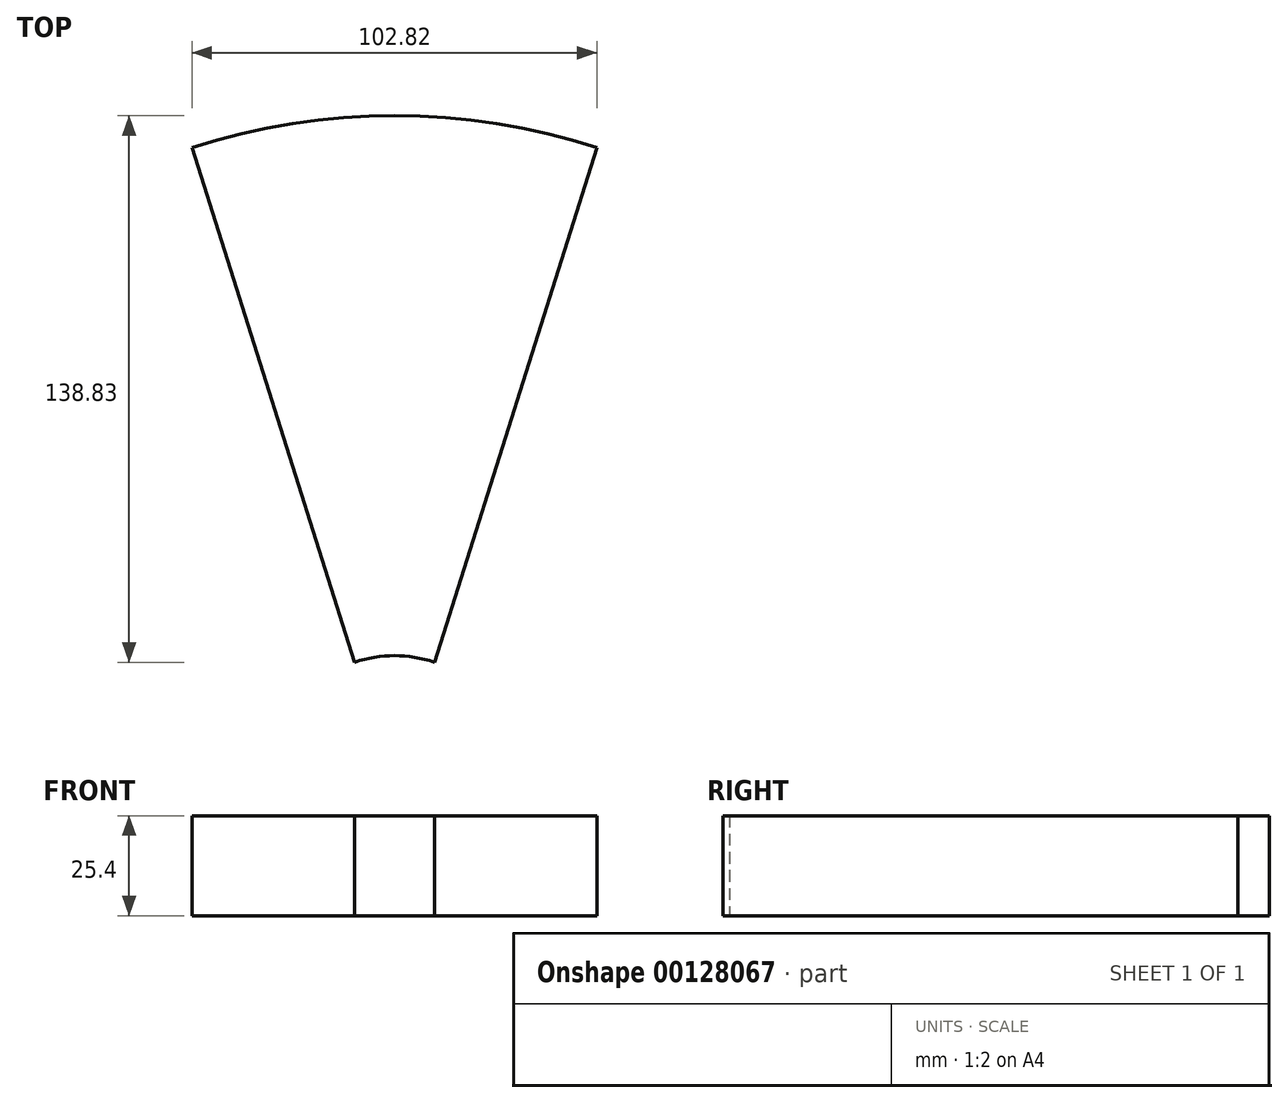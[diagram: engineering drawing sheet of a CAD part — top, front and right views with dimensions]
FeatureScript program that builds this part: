
annotation { "Feature Type Name" : "Feature", "Feature Type Description" : "" }
export const myFeature = defineFeature(function(context is Context, id is Id, definition is map)
    precondition{}
    {
        {
            var Q0;
            Q0=qCreatedBy(makeId("Top.planeOp"),FACE);
            var sketch = newSketch(context, id + "F0", { "sketchPlane" : qUnion([Q0])});
            skArc(sketch, "E0", {"start": v(10.16, 30.08) * mm, "mid": v(0, 31.75) * mm, "end": v(-10.16, 30.08) * mm});
            skArc(sketch, "E1", {"start": v(51.4, 160.9) * mm, "mid": v(0, 168.9) * mm, "end": v(-51.4, 160.9) * mm});
            skLineSegment(sketch, "E2", {"start": v(10.16, 30.08) * mm, "end": v(51.4, 160.9) * mm});
            skLineSegment(sketch, "E3", {"start": v(-51.4, 160.9) * mm, "end": v(-10.16, 30.08) * mm});
            skLineSegment(sketch, "E4", {"start": v(0, 0) * mm, "end": v(0, 96.4) * mm, "construction": true});
            skLineSegment(sketch, "E5", {"start": v(5.89, 37.64) * mm, "end": v(43.41, 156.66) * mm, "construction": true});
            skLineSegment(sketch, "E6", {"start": v(-43.41, 156.66) * mm, "end": v(-5.89, 37.64) * mm, "construction": true});
            skArc(sketch, "E7", {"start": v(-5.89, 37.64) * mm, "mid": v(0, 38.1) * mm, "end": v(5.89, 37.64) * mm, "construction": true});
            skArc(sketch, "E8", {"start": v(43.41, 156.66) * mm, "mid": v(0, 162.56) * mm, "end": v(-43.41, 156.66) * mm, "construction": true});
            skSolve(sketch);
        }
        {
            var Q0;
            Q0=makeQuery(id+"F0.imprint","IMPRINT",FACE,{"disambiguationData":[TD([[makeQuery(id+"F0.imprint","IMPRINT",EDGE,{"derivedFrom":sQuery(id+"F0.wireOp",EDGE,"E0")}),-1.0]])]});
            var Q1;
            Q1=makeQuery(id+"F0.imprint","IMPRINT",FACE,{"disambiguationData":[TD([[makeQuery(id+"F0.imprint","IMPRINT",EDGE,{"derivedFrom":sQuery(id+"F0.wireOp",EDGE,"E5")}),1.0]])]});
            extrude(context, id + "F1", {"entities" : qUnion([Q0, Q1]), "depth" : 25.4 * mm});
        }
    });
